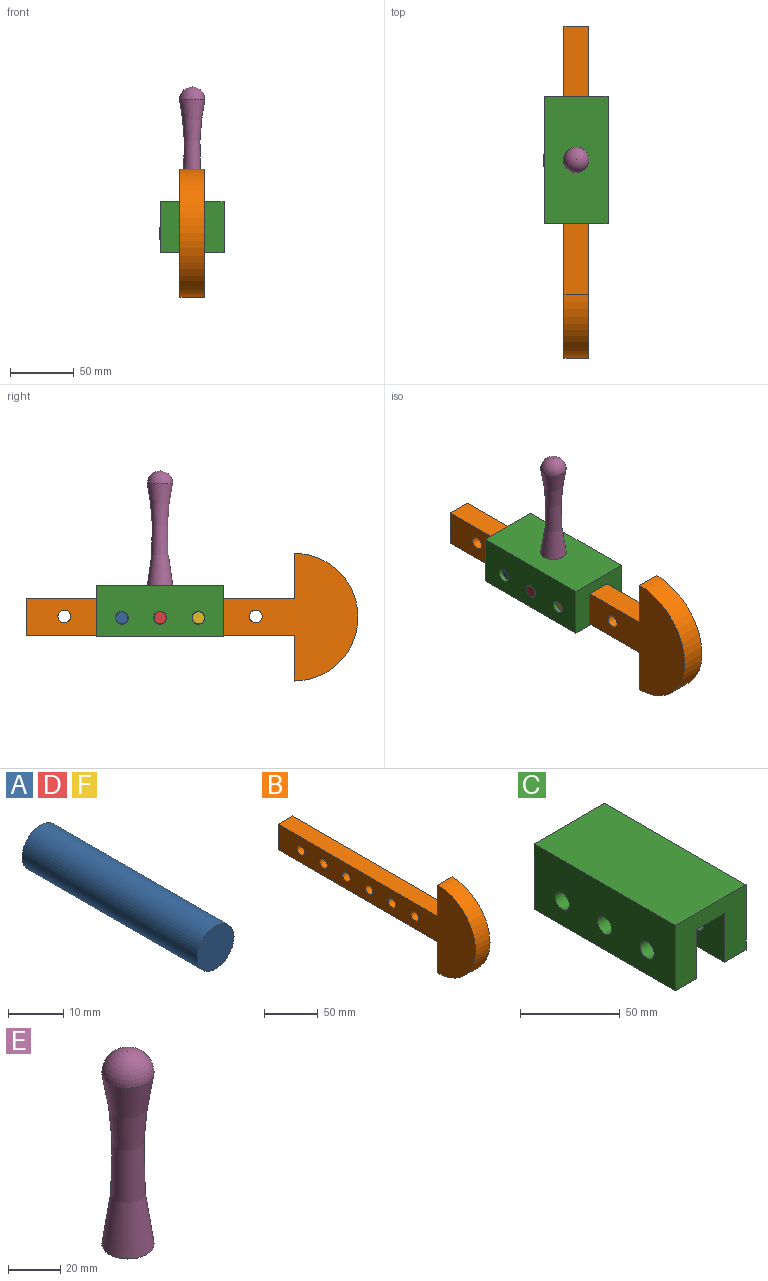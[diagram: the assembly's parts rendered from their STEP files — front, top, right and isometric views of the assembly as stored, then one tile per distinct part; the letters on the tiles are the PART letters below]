
ASSEMBLY  parts=6 mates=6
PART A: 3 faces, bbox 9.5x45x9.5 mm
  f0: cylinder r=4.75mm len=45mm, axis (0,1,0), area 1343mm2, adj f1,f2
  f1: plane 9.5x9.5mm, normal (0,-1,0), area 70.9mm2, adj f0
  f2: plane 9.5x9.5mm, normal (0,1,0), area 70.9mm2, adj f0
PART B: 14 faces, bbox 19x260x100 mm
  f0: plane 210x19mm, normal (0,0,1), area 3990mm2, adj f1,f3,f4,f12
  f1: plane 260x100mm, normal (-1,0,0), area 9545.8mm2, adj f0,f2,f4,f5,f6,f7,f8,f9
  f2: plane 210x19mm, normal (0,0,-1), area 3990mm2, adj f1,f3,f4,f11
  f3: plane 260x100mm, normal (1,0,0), area 9545.8mm2, adj f0,f2,f4,f5,f6,f7,f8,f9
  f4: plane 29x19mm, normal (0,1,0), area 551mm2, adj f0,f1,f2,f3
  f5: cylinder r=5mm len=19mm, axis (1,0,0), area 596.9mm2, adj f1,f3
  f6: cylinder r=5mm len=19mm, axis (1,0,0), area 596.9mm2, adj f1,f3
  f7: cylinder r=5mm len=19mm, axis (1,0,0), area 596.9mm2, adj f1,f3
  f8: cylinder r=5mm len=19mm, axis (1,0,0), area 596.9mm2, adj f1,f3
  f9: cylinder r=5mm len=19mm, axis (1,0,0), area 596.9mm2, adj f1,f3
  f10: cylinder r=5mm len=19mm, axis (1,0,0), area 596.9mm2, adj f1,f3
  f11: plane 35.5x19mm, normal (0,1,0), area 674.5mm2, adj f1,f2,f3,f13
  f12: plane 35.5x19mm, normal (0,1,0), area 674.5mm2, adj f0,f1,f3,f13
  f13: cylinder r=50mm len=100mm, axis (1,0,0), area 2984.5mm2, adj f1,f3,f11,f12
PART C: 16 faces, bbox 50x100x40 mm
  f0: plane 100x15mm, normal (0,0,-1), area 1500mm2, adj f1,f7,f8,f9
  f1: plane 100x30mm, normal (1,0,0), area 2764.4mm2, adj f0,f2,f8,f9,f10,f11,f12
  f2: plane 100x20mm, normal (0,0,-1), area 2000mm2, adj f1,f3,f8,f9
  f3: plane 100x30mm, normal (-1,0,0), area 2764.4mm2, adj f2,f4,f8,f9,f13,f14,f15
  f4: plane 100x15mm, normal (0,0,-1), area 1500mm2, adj f3,f5,f8,f9
  f5: plane 100x40mm, normal (1,0,0), area 3764.4mm2, adj f4,f6,f8,f9,f13,f14,f15
  f6: plane 100x50mm, normal (0,0,1), area 5000mm2, adj f5,f7,f8,f9
  f7: plane 100x40mm, normal (-1,0,0), area 3764.4mm2, adj f0,f6,f8,f9,f10,f11,f12
  f8: plane 50x40mm, normal (0,-1,0), area 1400mm2, adj f0,f1,f2,f3,f4,f5,f6,f7
  f9: plane 50x40mm, normal (0,1,0), area 1400mm2, adj f0,f1,f2,f3,f4,f5,f6,f7
  f10: cylinder r=5mm len=15mm, axis (1,0,0), area 471.2mm2, adj f1,f7
  f11: cylinder r=5mm len=15mm, axis (1,0,0), area 471.2mm2, adj f1,f7
  f12: cylinder r=5mm len=15mm, axis (1,0,0), area 471.2mm2, adj f1,f7
  f13: cylinder r=5mm len=15mm, axis (1,0,0), area 471.2mm2, adj f3,f5
  f14: cylinder r=5mm len=15mm, axis (1,0,0), area 471.2mm2, adj f3,f5
  f15: cylinder r=5mm len=15mm, axis (1,0,0), area 471.2mm2, adj f3,f5
PART D: same geometry as A
PART E: 3 faces, bbox 138.5x138.5x284 mm
  f0: plane 20x20mm, normal (0,0,-1), area 314.2mm2, adj f2
  f1: sphere r=10mm, area 628.3mm2, adj f2
  f2: torus R=205.96mm, axis (0,0,-1), area 3698.3mm2, adj f0,f1
PART F: same geometry as A
PLACE A rot(axis=(-0.58,0.58,0.58),120deg) t=(-68.15,41.94,8.44)mm
PLACE B rot(axis=(0,1,0),180deg) t=(-62.26,116.94,14.36)mm
PLACE C t=(-46.71,61.94,13.44)mm
PLACE D rot(axis=(-0.58,-0.58,-0.58),120deg) t=(-26.89,11.94,8.44)mm
PLACE E t=(-46.71,61.94,13.27)mm fixed
PLACE F rot(axis=(0.58,-0.58,0.58),120deg) t=(-68.7,-18.06,8.44)mm
MATE fastened C.f6 <-> E.f2  axis (0,0,1) through (-46.71,11.94,33.44)mm
MATE slider F.f0 <-> C.f12  axis (-1,0,0) through (-68.7,-18.06,8.44)mm
MATE slider C.f11 <-> C.f11  axis (1,0,0) through (-21.71,11.94,8.44)mm
MATE slider C.f10 <-> A.f0  axis (1,0,0) through (-21.71,41.94,8.44)mm
MATE parallel B.f2 <-> C.f2  axis (0,0,1) through (-46.71,11.94,23.44)mm
MATE slider D.f0 <-> C.f11  axis (1,0,0) through (-26.89,11.94,8.44)mm
